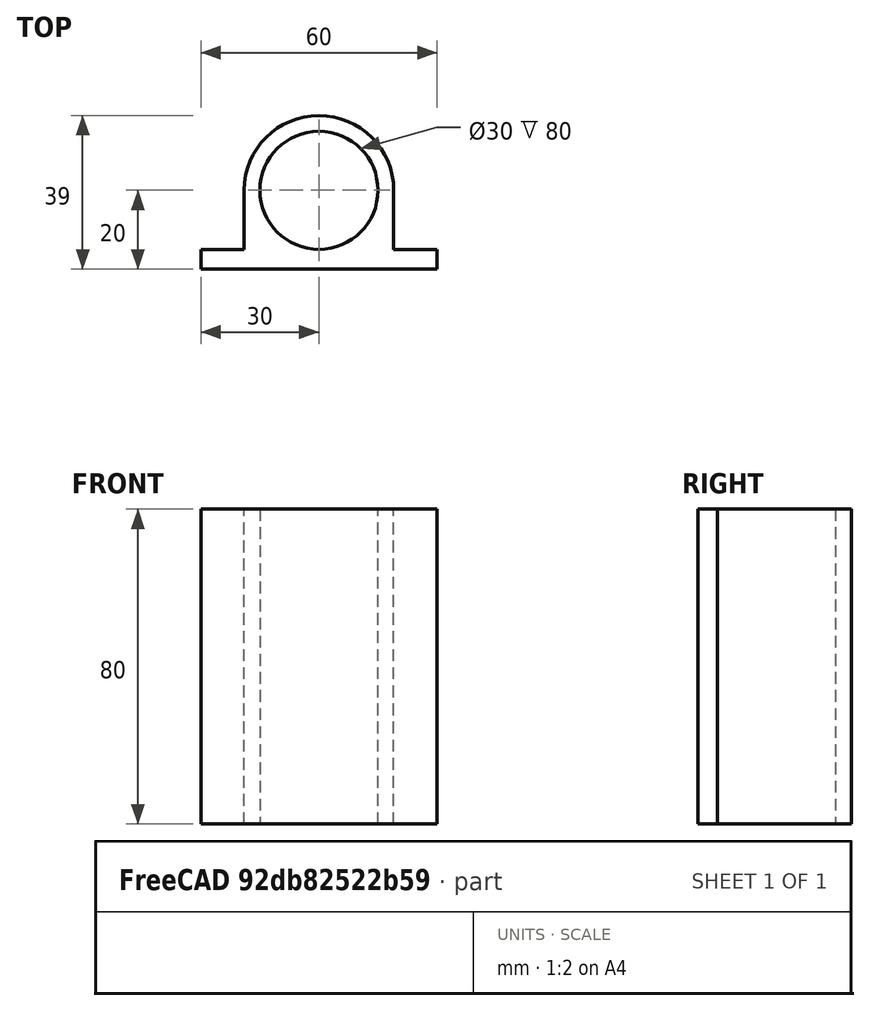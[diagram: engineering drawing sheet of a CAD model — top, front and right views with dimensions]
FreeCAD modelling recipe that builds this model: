
FCSTD DOCUMENT  (FreeCAD 0.17RUnknown)
Label: holder2
License: All rights reserved
LicenseURL: http://en.wikipedia.org/wiki/All_rights_reserved
objects: Sketcher::SketchObject×1, PartDesign::Pad×1, PartDesign::Body×1
note: 4 computed .brp shape members not serialized (recipe doc carries the construction recipe); baked Part::Feature solids carry a one-line shape summary decoded from their .brp

FEATURE [Sketcher::SketchObject] Sketch
  MapMode = 5
  sketch-geometry (9):
    g0: LineSegment StartX=30 StartY=5 StartZ=0 EndX=30 EndY=0 EndZ=0
    g1: LineSegment StartX=30 StartY=0 StartZ=0 EndX=-30 EndY=0 EndZ=0
    g2: LineSegment StartX=-30 StartY=0 StartZ=0 EndX=-30 EndY=5 EndZ=0
    g3: LineSegment StartX=-19 StartY=20 StartZ=0 EndX=-19 EndY=5 EndZ=0
    g4: LineSegment StartX=19 StartY=20 StartZ=0 EndX=19 EndY=5 EndZ=0
    g5: ArcOfCircle CenterX=0 CenterY=20 CenterZ=0 NormalX=0 NormalY=0 NormalZ=1 AngleXU=0 Radius=19 StartAngle=0 EndAngle=3.14159
    g6: LineSegment StartX=-30 StartY=5 StartZ=0 EndX=-19 EndY=5 EndZ=0
    g7: LineSegment StartX=19 StartY=5 StartZ=0 EndX=30 EndY=5 EndZ=0
    g8: Circle CenterX=0 CenterY=20 CenterZ=0 NormalX=0 NormalY=0 NormalZ=1 AngleXU=0 Radius=15
  constraints (24):
    c: Coincident(g0,g1)
    c: Coincident(g1,g2)
    c: Coincident(g5,g4)
    c: Coincident(g3,g5)
    c: Coincident(g6,g2)
    c: Coincident(g6,g3)
    c: Coincident(g7,g0)
    c: Coincident(g8,g5)
    c: Coincident(g4,g7)
    c: PointOnObject(g0,g-1)
    c: PointOnObject(g5,g-2)
    c: Symmetric(g2,g0,g-2)
    c: Symmetric(g3,g4,g-2)
    c: Symmetric(g4,g3,g-2)
    c: Symmetric(g0,g1,g-2)
    c: Parallel(g0,g-2)
    c: Parallel(g7,g-1)
    c: Parallel(g4,g-2)
    c: Angle(g5) = 3.14159
    c: Distance(g0) = 5
    c: Radius(g8) = 15
    c: Radius(g5) = 19
    c: Distance(g4) = 15
    c: Distance(g-1,g0) = 30
FEATURE [PartDesign::Pad] Pad
  Length = 80
  Length2 = 100
  Profile = -> Sketch
  Type = 0
FEATURE [PartDesign::Body] Body
  Group = -> [Sketch,Pad]
  Origin = -> Origin
  Tip = -> Pad
